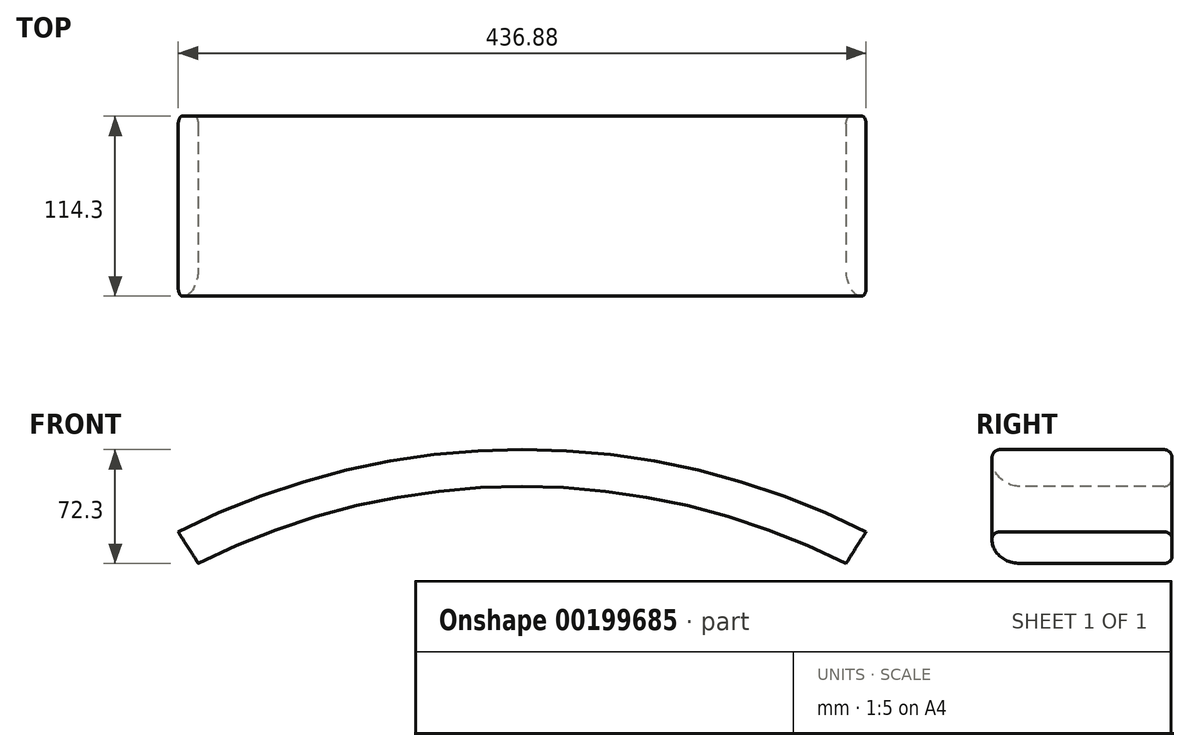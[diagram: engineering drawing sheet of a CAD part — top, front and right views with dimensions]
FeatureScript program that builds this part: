
annotation { "Feature Type Name" : "Feature", "Feature Type Description" : "" }
export const myFeature = defineFeature(function(context is Context, id is Id, definition is map)
    precondition{}
    {
        {
            var Q0;
            Q0=qCreatedBy(makeId("Front.planeOp"),FACE);
            var sketch = newSketch(context, id + "F0", { "sketchPlane" : qUnion([Q0])});
            skLineSegment(sketch, "E0", {"start": v(0, 260.35) * mm, "end": v(0, -260.35) * mm, "construction": true});
            skPoint(sketch, "E1", {"position": v(-218.44, 133.5) * mm});
            skPoint(sketch, "E2", {"position": v(218.44, 133.5) * mm});
            skLineSegment(sketch, "E3", {"start": v(-218.44, 133.5) * mm, "end": v(-205.74, 113.46) * mm});
            skLineSegment(sketch, "E4", {"start": v(218.44, 133.5) * mm, "end": v(205.74, 113.46) * mm});
            skArc(sketch, "E5", {"start": v(205.74, 113.46) * mm, "mid": v(0, 162.36) * mm, "end": v(-205.74, 113.46) * mm});
            skArc(sketch, "E6", {"start": v(218.44, 133.5) * mm, "mid": v(0, 185.76) * mm, "end": v(-218.44, 133.5) * mm});
            skPoint(sketch, "E7.center.orphan", {"position": v(0, 0) * mm});
            skSolve(sketch);
        }
        {
            var Q0;
            Q0=makeQuery(id+"F0.imprint","IMPRINT",FACE,{"disambiguationData":[TD([[makeQuery(id+"F0.imprint","IMPRINT",EDGE,{"derivedFrom":sQuery(id+"F0.wireOp",EDGE,"E3")}),1.0]])]});
            extrude(context, id + "F1", {"entities" : qUnion([Q0]), "oppositeDirection" : true, "depth" : 114.3 * mm});
        }
        {
            var Q0;
            Q0=makeQuery(id+"F1.opExtrude","CAP_EDGE",EDGE,{"disambiguationData":[OSD([sQuery(id+"F0.wireOp",EDGE,"E6")])],"isStart":true});
            var Q1;
            Q1=makeQuery(id+"F1.opExtrude","CAP_EDGE",EDGE,{"disambiguationData":[OSD([sQuery(id+"F0.wireOp",EDGE,"E5")])],"isStart":false});
            var Q2;
            Q2=makeQuery(id+"F1.opExtrude","CAP_EDGE",EDGE,{"disambiguationData":[OSD([sQuery(id+"F0.wireOp",EDGE,"E6")])],"isStart":false});
            fillet(context, id + "F2", {"entities" : qUnion([Q0, Q1, Q2]), "radius" : 5.08 * mm, "tangentPropagation" : true, "allowEdgeOverflow" : false});
        }
        {
            var Q0;
            Q0=makeQuery(id+"F1.opExtrude","CAP_EDGE",EDGE,{"disambiguationData":[OSD([sQuery(id+"F0.wireOp",EDGE,"E5")])],"isStart":true});
            fillet(context, id + "F3", {"entities" : qUnion([Q0]), "radius" : 17.78 * mm, "allowEdgeOverflow" : false});
        }
    });
